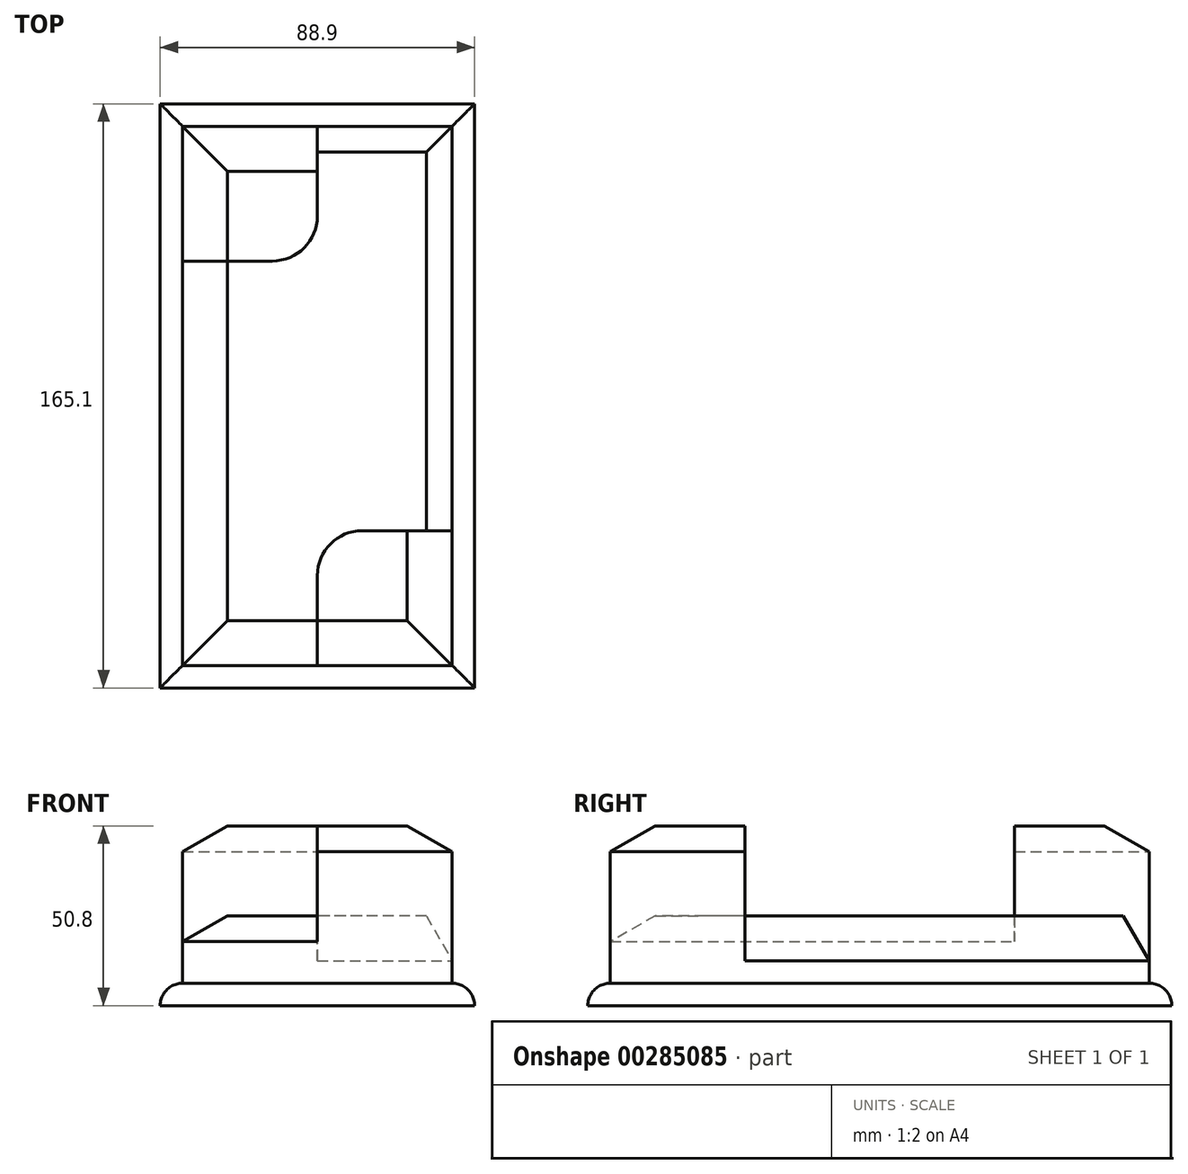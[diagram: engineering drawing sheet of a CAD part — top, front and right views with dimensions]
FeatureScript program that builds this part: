
annotation { "Feature Type Name" : "Feature", "Feature Type Description" : "" }
export const myFeature = defineFeature(function(context is Context, id is Id, definition is map)
    precondition{}
    {
        {
            var Q0;
            Q0=qCreatedBy(makeId("Top.planeOp"),FACE);
            var sketch = newSketch(context, id + "F0", { "sketchPlane" : qUnion([Q0])});
            skLineSegment(sketch, "E0.bottom", {"start": v(-38.1, 43.22) * mm, "end": v(38.1, 43.22) * mm});
            skLineSegment(sketch, "E0.top", {"start": v(-38.1, -109.18) * mm, "end": v(38.1, -109.18) * mm});
            skLineSegment(sketch, "E0.left", {"start": v(-38.1, 43.22) * mm, "end": v(-38.1, -109.18) * mm});
            skLineSegment(sketch, "E0.right", {"start": v(38.1, 43.22) * mm, "end": v(38.1, -109.18) * mm});
            skLineSegment(sketch, "E1.0", {"start": v(-44.45, 49.57) * mm, "end": v(44.45, 49.57) * mm});
            skLineSegment(sketch, "E1.1", {"start": v(-44.45, 49.57) * mm, "end": v(-44.45, -115.53) * mm});
            skLineSegment(sketch, "E1.2", {"start": v(-44.45, -115.53) * mm, "end": v(44.45, -115.53) * mm});
            skLineSegment(sketch, "E1.3", {"start": v(44.45, 49.57) * mm, "end": v(44.45, -115.53) * mm});
            skLineSegment(sketch, "E2.top", {"start": v(-38.1, 5.12) * mm, "end": v(-12.7, 5.12) * mm});
            skLineSegment(sketch, "E2.right", {"start": v(0, 43.22) * mm, "end": v(0, 17.82) * mm});
            skLineSegment(sketch, "E3.top", {"start": v(38.1, -71.08) * mm, "end": v(12.7, -71.08) * mm});
            skLineSegment(sketch, "E3.right", {"start": v(0, -109.18) * mm, "end": v(0, -83.78) * mm});
            skPoint(sketch, "E4.visualSharp", {"position": v(0, 5.12) * mm});
            skArc(sketch, "E4.filletArc", {"start": v(-12.7, 5.12) * mm, "mid": v(-3.72, 8.84) * mm, "end": v(0, 17.82) * mm});
            skPoint(sketch, "E5.visualSharp", {"position": v(0, -71.08) * mm});
            skArc(sketch, "E5.filletArc", {"start": v(12.7, -71.08) * mm, "mid": v(3.72, -74.8) * mm, "end": v(0, -83.78) * mm});
            skSolve(sketch);
        }
        {
            var Q0;
            Q0=makeQuery(id+"F0.imprint","IMPRINT",FACE,{"disambiguationData":[TD([[makeQuery(id+"F0.imprint","IMPRINT",EDGE,{"derivedFrom":sQuery(id+"F0.wireOp",EDGE,"E0.bottom")}),1.0]])]});
            extrude(context, id + "F1", {"entities" : qUnion([Q0]), "depth" : 6.35 * mm});
        }
        {
            var Q0;
            Q0=makeQuery(id+"F0.imprint","IMPRINT",FACE,{"disambiguationData":[TD([[makeQuery(id+"F0.imprint","IMPRINT",EDGE,{"derivedFrom":sQuery(id+"F0.wireOp",EDGE,"E0.bottom")}),-1.0]])]});
            var Q1;
            {var subQ1=sQuery(id+"F0.wireOp",EDGE,"E3.top");Q1=makeQuery(id+"F0.imprint","IMPRINT",FACE,{"disambiguationData":[TD([[makeQuery(id+"F0.imprint","IMPRINT",EDGE,{"derivedFrom":subQ1}),1.0]])]});}
            extrude(context, id + "F2", {"entities" : qUnion([Q0, Q1]), "operationType" : NewBodyOperationType.ADD, "depth" : 50.8 * mm});
        }
        {
            var Q0;
            {var subQ3=sQuery(id+"F0.wireOp",EDGE,"E2.top");Q0=makeQuery(id+"F0.imprint","IMPRINT",FACE,{"disambiguationData":[TD([[makeQuery(id+"F0.imprint","IMPRINT",EDGE,{"derivedFrom":subQ3}),-1.0]])]});}
            extrude(context, id + "F3", {"entities" : qUnion([Q0]), "operationType" : NewBodyOperationType.ADD, "depth" : 25.4 * mm});
        }
        {
            var Q0;
            Q0=makeQuery(id+"F1.opExtrude","CAP_EDGE",EDGE,{"disambiguationData":[OSD([sQuery(id+"F0.wireOp",EDGE,"E1.3")])],"isStart":false});
            var Q1;
            Q1=makeQuery(id+"F1.opExtrude","CAP_EDGE",EDGE,{"disambiguationData":[OSD([sQuery(id+"F0.wireOp",EDGE,"E1.0")])],"isStart":false});
            var Q2;
            Q2=makeQuery(id+"F1.opExtrude","CAP_EDGE",EDGE,{"disambiguationData":[OSD([sQuery(id+"F0.wireOp",EDGE,"E1.2")])],"isStart":false});
            var Q3;
            Q3=makeQuery(id+"F1.opExtrude","CAP_EDGE",EDGE,{"disambiguationData":[OSD([sQuery(id+"F0.wireOp",EDGE,"E1.1")])],"isStart":false});
            fillet(context, id + "F4", {"entities" : qUnion([Q0, Q1, Q2, Q3]), "radius" : 6.35 * mm, "tangentPropagation" : true, "allowEdgeOverflow" : false});
        }
        {
            var Q0;
            Q0=makeQuery(id+"F2.opExtrude","CAP_EDGE",EDGE,{"disambiguationData":[OSD([sQuery(id+"F0.wireOp",EDGE,"E0.left")])],"isStart":false});
            var Q1;
            Q1=makeQuery(id+"F2.opExtrude","CAP_EDGE",EDGE,{"disambiguationData":[OSD([sQuery(id+"F0.wireOp",EDGE,"E0.bottom")])],"isStart":false});
            var Q2;
            Q2=makeQuery(id+"F3.opExtrude","CAP_EDGE",EDGE,{"disambiguationData":[OSD([sQuery(id+"F0.wireOp",EDGE,"E0.right")])],"isStart":false});
            var Q3;
            Q3=makeQuery(id+"F3.opExtrude","CAP_EDGE",EDGE,{"disambiguationData":[OSD([sQuery(id+"F0.wireOp",EDGE,"E0.bottom")])],"isStart":false});
            var Q4;
            Q4=makeQuery(id+"F3.opExtrude","CAP_EDGE",EDGE,{"disambiguationData":[OSD([sQuery(id+"F0.wireOp",EDGE,"E0.left")])],"isStart":false});
            var Q5;
            Q5=makeQuery(id+"F3.opExtrude","CAP_EDGE",EDGE,{"disambiguationData":[OSD([sQuery(id+"F0.wireOp",EDGE,"E0.top")])],"isStart":false});
            chamfer(context, id + "F5", {"entities" : qUnion([Q0, Q1, Q2, Q3, Q4, Q5]), "chamferType" : ChamferType.OFFSET_ANGLE, "width" : 12.7 * mm, "oppositeDirection" : false, "angle" : 30 * degree, "tangentPropagation" : true});
        }
        {
            var Q0;
            Q0=makeQuery(id+"F2.opExtrude","CAP_EDGE",EDGE,{"disambiguationData":[OSD([sQuery(id+"F0.wireOp",EDGE,"E0.top")])],"isStart":false});
            var Q1;
            Q1=makeQuery(id+"F2.opExtrude","CAP_EDGE",EDGE,{"disambiguationData":[OSD([sQuery(id+"F0.wireOp",EDGE,"E0.right")])],"isStart":false});
            chamfer(context, id + "F6", {"entities" : qUnion([Q0, Q1]), "chamferType" : ChamferType.OFFSET_ANGLE, "width" : 12.7 * mm, "oppositeDirection" : false, "angle" : 30 * degree, "tangentPropagation" : true});
        }
    });
